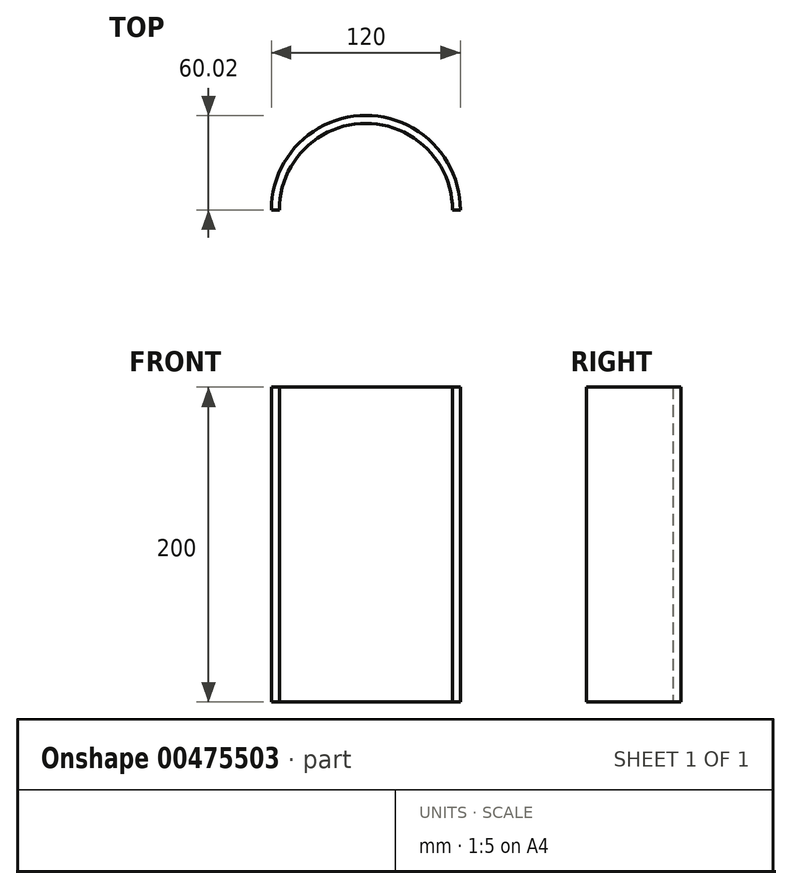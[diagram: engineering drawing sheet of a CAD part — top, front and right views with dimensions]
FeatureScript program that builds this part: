
annotation { "Feature Type Name" : "Feature", "Feature Type Description" : "" }
export const myFeature = defineFeature(function(context is Context, id is Id, definition is map)
    precondition{}
    {
        {
            var Q0;
            Q0=qCreatedBy(makeId("Top.planeOp"),FACE);
            var sketch = newSketch(context, id + "F0", { "sketchPlane" : qUnion([Q0])});
            skArc(sketch, "E0", {"start": v(55, -0.02) * mm, "mid": v(0.01, 55) * mm, "end": v(-55, 0) * mm});
            skArc(sketch, "E1", {"start": v(60, -0.02) * mm, "mid": v(0.01, 60) * mm, "end": v(-60, 0) * mm});
            skLineSegment(sketch, "E2", {"start": v(-55, 0) * mm, "end": v(-60, 0) * mm});
            skLineSegment(sketch, "E3", {"start": v(55, -0.02) * mm, "end": v(60, -0.02) * mm});
            skSolve(sketch);
        }
        {
            var Q0;
            Q0=makeQuery(id+"F0.imprint","IMPRINT",FACE,{"disambiguationData":[TD([[makeQuery(id+"F0.imprint","IMPRINT",EDGE,{"derivedFrom":sQuery(id+"F0.wireOp",EDGE,"E0")}),-1.0]])]});
            extrude(context, id + "F1", {"entities" : qUnion([Q0]), "depth" : 200 * mm, "offsetDistance" : 25 * mm});
        }
    });
